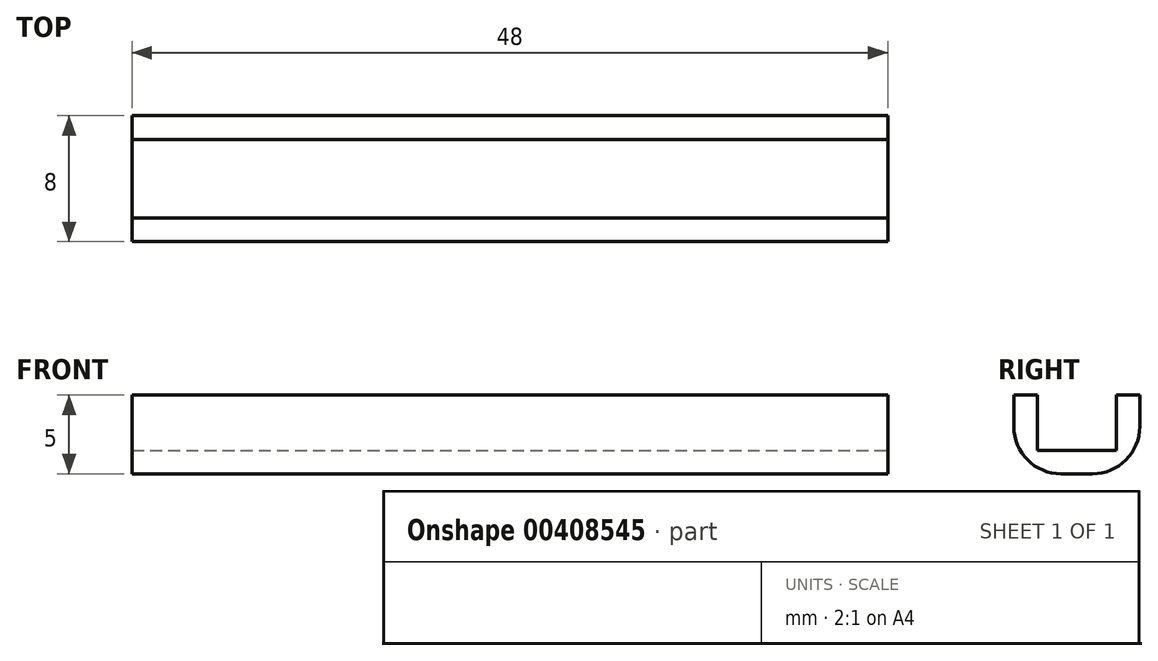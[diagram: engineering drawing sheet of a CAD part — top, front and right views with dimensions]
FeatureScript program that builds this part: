
annotation { "Feature Type Name" : "Feature", "Feature Type Description" : "" }
export const myFeature = defineFeature(function(context is Context, id is Id, definition is map)
    precondition{}
    {
        {
            var Q0;
            Q0=qCreatedBy(makeId("Top.planeOp"),FACE);
            var sketch = newSketch(context, id + "F0", { "sketchPlane" : qUnion([Q0])});
            skLineSegment(sketch, "E0.bottom", {"start": v(-24, 4) * mm, "end": v(24, 4) * mm});
            skLineSegment(sketch, "E0.top", {"start": v(-24, -4) * mm, "end": v(24, -4) * mm});
            skLineSegment(sketch, "E0.left", {"start": v(-24, 4) * mm, "end": v(-24, -4) * mm});
            skLineSegment(sketch, "E0.right", {"start": v(24, 4) * mm, "end": v(24, -4) * mm});
            skPoint(sketch, "E0.middle", {"position": v(0, 0) * mm});
            skSolve(sketch);
        }
        {
            var Q0;
            Q0=makeQuery(id+"F0.imprint","IMPRINT",FACE,{"disambiguationData":[TD([[makeQuery(id+"F0.imprint","IMPRINT",EDGE,{"derivedFrom":sQuery(id+"F0.wireOp",EDGE,"E0.bottom")}),-1.0]])]});
            extrude(context, id + "F1", {"entities" : qUnion([Q0]), "depth" : 5 * mm});
        }
        {
            var Q0;
            Q0=makeQuery(id+"F1.opExtrude","CAP_FACE",FACE,{"disambiguationData":[OSD([sQuery(id+"F0.wireOp",EDGE,"E0.bottom"),sQuery(id+"F0.wireOp",EDGE,"E0.top"),sQuery(id+"F0.wireOp",EDGE,"E0.left"),sQuery(id+"F0.wireOp",EDGE,"E0.right")])],"isStart":false});
            var sketch = newSketch(context, id + "F2", { "sketchPlane" : qUnion([Q0])});
            skLineSegment(sketch, "E1.bottom", {"start": v(-24, 2.5) * mm, "end": v(24, 2.5) * mm});
            skLineSegment(sketch, "E1.top", {"start": v(-24, -2.5) * mm, "end": v(24, -2.5) * mm});
            skLineSegment(sketch, "E1.left", {"start": v(-24, 2.5) * mm, "end": v(-24, -2.5) * mm});
            skLineSegment(sketch, "E1.right", {"start": v(24, 2.5) * mm, "end": v(24, -2.5) * mm});
            skSolve(sketch);
        }
        {
            var Q0;
            Q0=makeQuery(id+"F2.imprint","IMPRINT",FACE,{"disambiguationData":[TD([[makeQuery(id+"F2.imprint","IMPRINT",EDGE,{"derivedFrom":sQuery(id+"F2.wireOp",EDGE,"E1.bottom")}),-1.0]])]});
            extrude(context, id + "F3", {"entities" : qUnion([Q0]), "operationType" : NewBodyOperationType.REMOVE, "oppositeDirection" : true, "depth" : 3.5 * mm});
        }
        {
            var Q0;
            Q0=makeQuery(id+"F1.opExtrude","CAP_EDGE",EDGE,{"disambiguationData":[OSD([sQuery(id+"F0.wireOp",EDGE,"E0.top")])],"isStart":true});
            var Q1;
            Q1=makeQuery(id+"F1.opExtrude","CAP_EDGE",EDGE,{"disambiguationData":[OSD([sQuery(id+"F0.wireOp",EDGE,"E0.bottom")])],"isStart":true});
            fillet(context, id + "F4", {"entities" : qUnion([Q0, Q1]), "radius" : 3 * mm, "tangentPropagation" : true, "allowEdgeOverflow" : false});
        }
    });
